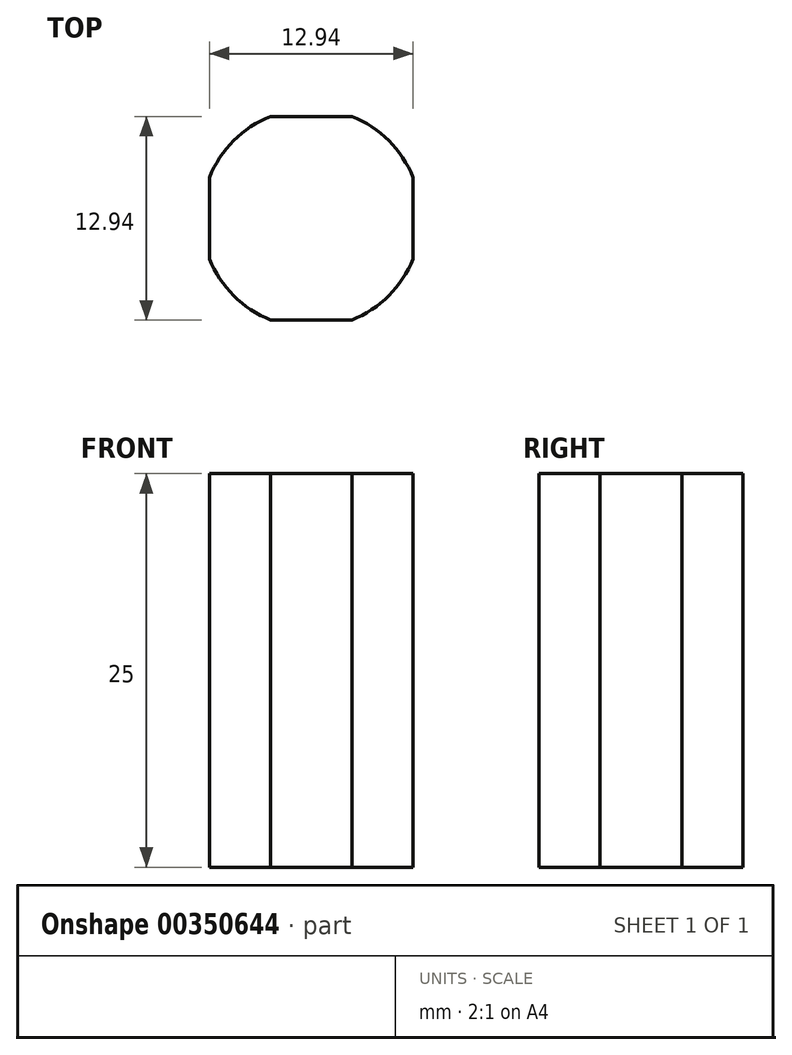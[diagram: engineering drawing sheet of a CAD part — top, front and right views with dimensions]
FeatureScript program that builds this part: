
annotation { "Feature Type Name" : "Feature", "Feature Type Description" : "" }
export const myFeature = defineFeature(function(context is Context, id is Id, definition is map)
    precondition{}
    {
        {
            var Q0;
            Q0=qCreatedBy(makeId("Top.planeOp"),FACE);
            var sketch = newSketch(context, id + "F0", { "sketchPlane" : qUnion([Q0])});
            skCircle(sketch, "E0", {"center": v(0, 0) * mm, "radius": 6.96 * mm});
            skLineSegment(sketch, "E1.bottom", {"start": v(6.46, -6.47) * mm, "end": v(-6.47, -6.47) * mm});
            skLineSegment(sketch, "E1.top", {"start": v(6.47, 6.47) * mm, "end": v(-6.47, 6.47) * mm});
            skLineSegment(sketch, "E1.left", {"start": v(6.46, -6.47) * mm, "end": v(6.47, 6.47) * mm});
            skLineSegment(sketch, "E1.right", {"start": v(-6.47, -6.47) * mm, "end": v(-6.47, 6.47) * mm});
            skSolve(sketch);
        }
        {
            var Q0;
            {var subQ1=sQuery(id+"F0.wireOp",EDGE,"E0");var subQ9=sQuery(id+"F0.wireOp",EDGE,"E1.top");var subQ12=makeQuery(id+"F0.imprint","INTERSECT",VERTEX,{"disambiguationData":[OD(0.0)],"derivedFrom":[subQ1,subQ9]});Q0=makeQuery(id+"F0.imprint","IMPRINT",FACE,{"disambiguationData":[TD([[makeQuery(id+"F0.imprint","IMPRINT",EDGE,{"disambiguationData":[TD([[subQ12,1.0]])],"derivedFrom":subQ1}),1.0]])]});}
            extrude(context, id + "F1", {"entities" : qUnion([Q0]), "depth" : 25 * mm});
        }
    });
